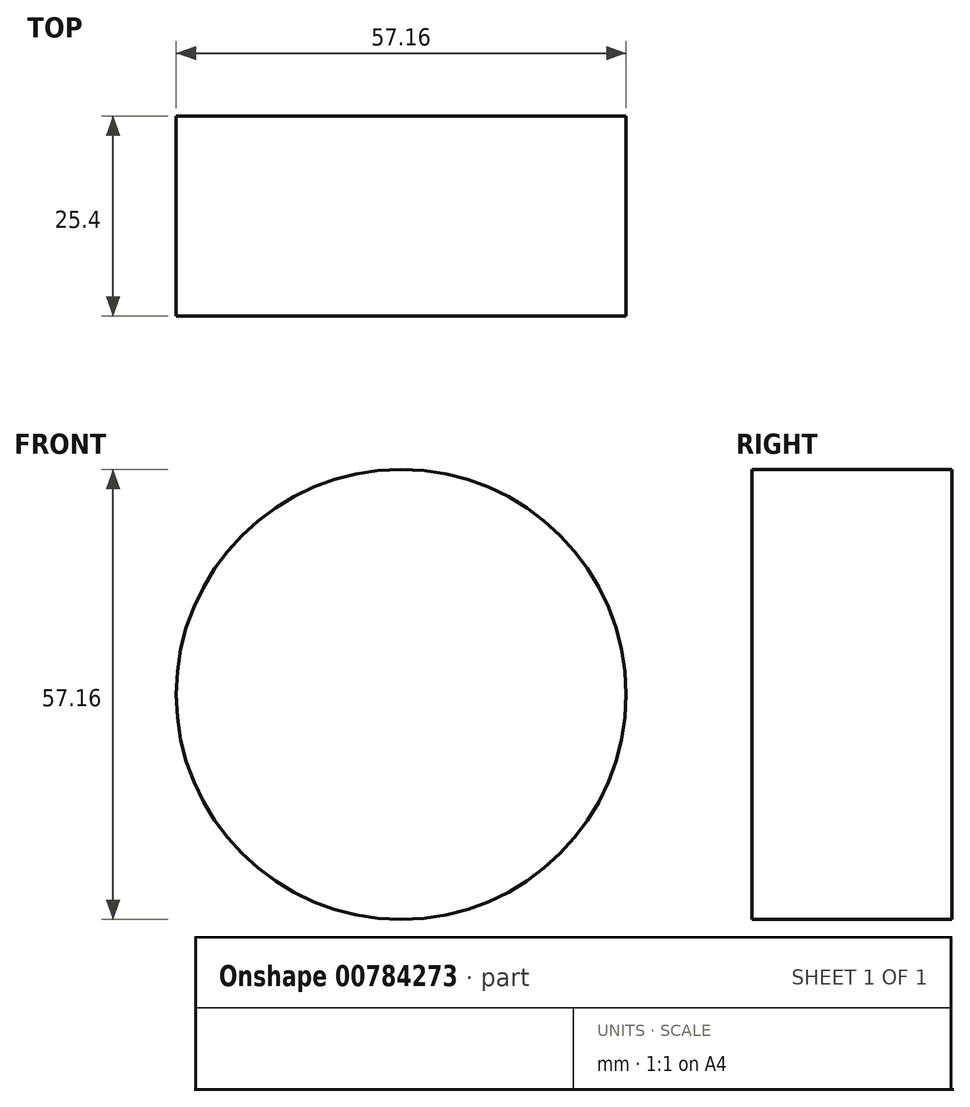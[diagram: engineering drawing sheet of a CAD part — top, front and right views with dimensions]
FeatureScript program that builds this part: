
annotation { "Feature Type Name" : "Feature", "Feature Type Description" : "" }
export const myFeature = defineFeature(function(context is Context, id is Id, definition is map)
    precondition{}
    {
        {
            var Q0;
            Q0=qCreatedBy(makeId("Front.planeOp"),FACE);
            var sketch = newSketch(context, id + "F0", { "sketchPlane" : qUnion([Q0])});
            skCircle(sketch, "E0", {"center": v(0, 0) * mm, "radius": 28.58 * mm});
            skSolve(sketch);
        }
        {
            var Q0;
            Q0 = qSketchRegion(id + "F0", true);
            extrude(context, id + "F1", {"entities" : qUnion([Q0]), "depth" : 25.4 * mm, "offsetDistance" : 25.4 * mm});
        }
    });
